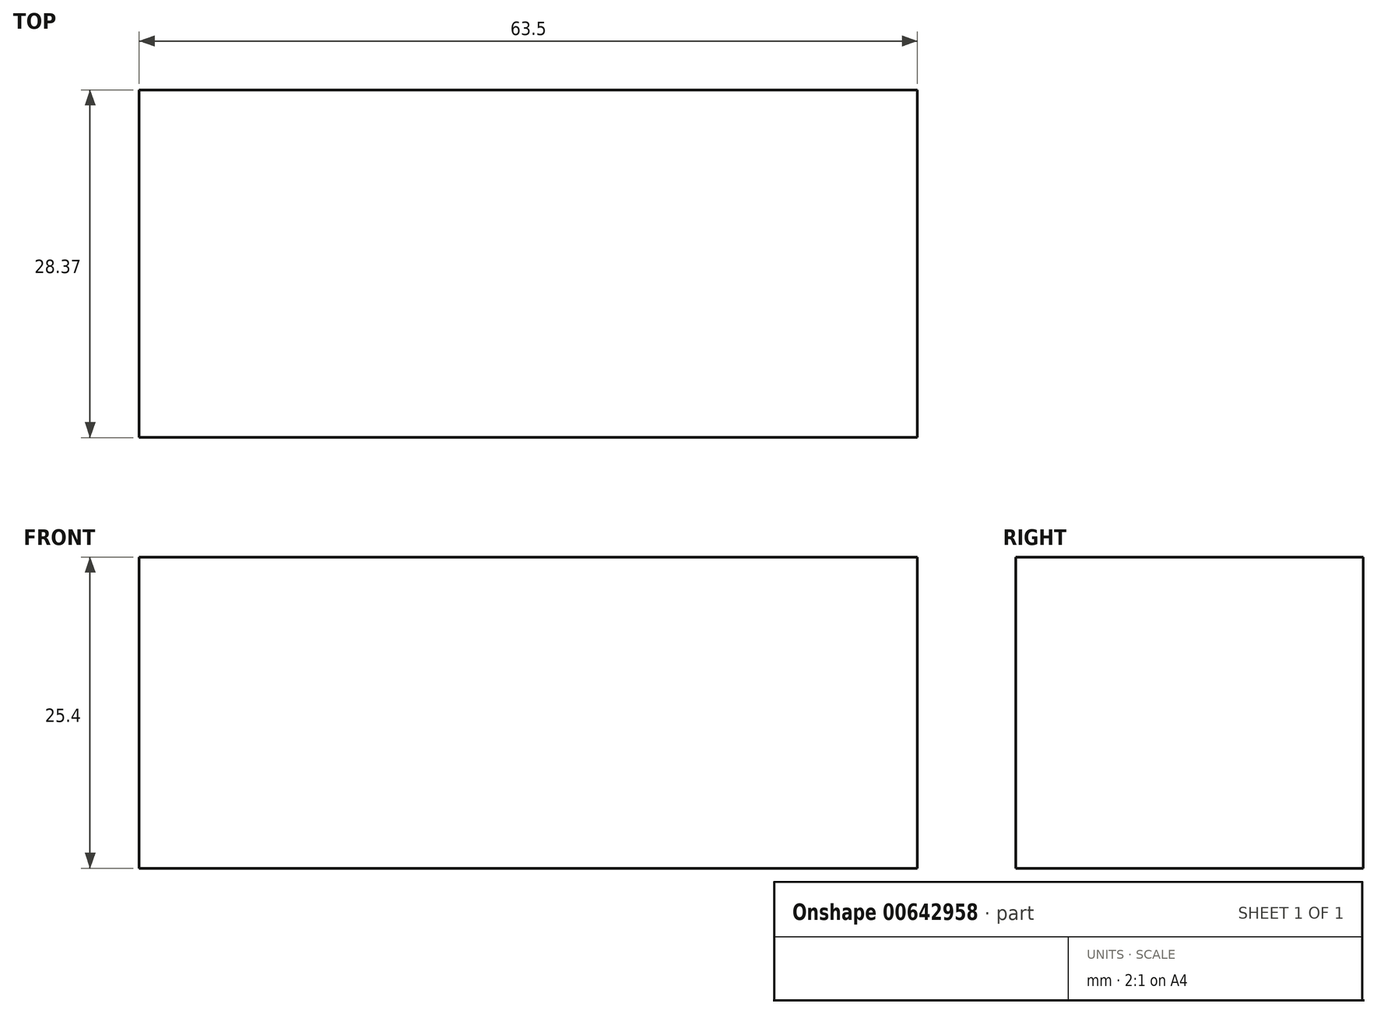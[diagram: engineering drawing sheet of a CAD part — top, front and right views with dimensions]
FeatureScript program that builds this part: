
annotation { "Feature Type Name" : "Feature", "Feature Type Description" : "" }
export const myFeature = defineFeature(function(context is Context, id is Id, definition is map)
    precondition{}
    {
        {
            var Q0;
            Q0=qCreatedBy(makeId("Top.planeOp"),FACE);
            var sketch = newSketch(context, id + "F0", { "sketchPlane" : qUnion([Q0])});
            skLineSegment(sketch, "E0.bottom", {"start": v(0, 0) * mm, "end": v(-63.5, 0) * mm});
            skLineSegment(sketch, "E0.top", {"start": v(0, -28.37) * mm, "end": v(-63.5, -28.37) * mm});
            skLineSegment(sketch, "E0.left", {"start": v(0, 0) * mm, "end": v(0, -28.37) * mm});
            skLineSegment(sketch, "E0.right", {"start": v(-63.5, 0) * mm, "end": v(-63.5, -28.37) * mm});
            skSolve(sketch);
        }
        {
            var Q0;
            Q0=makeQuery(id+"F0.imprint","IMPRINT",FACE,{"disambiguationData":[TD([[makeQuery(id+"F0.imprint","IMPRINT",EDGE,{"derivedFrom":sQuery(id+"F0.wireOp",EDGE,"E0.bottom")}),1.0]])]});
            extrude(context, id + "F1", {"entities" : qUnion([Q0]), "depth" : 25.4 * mm, "offsetDistance" : 25.4 * mm});
        }
    });
